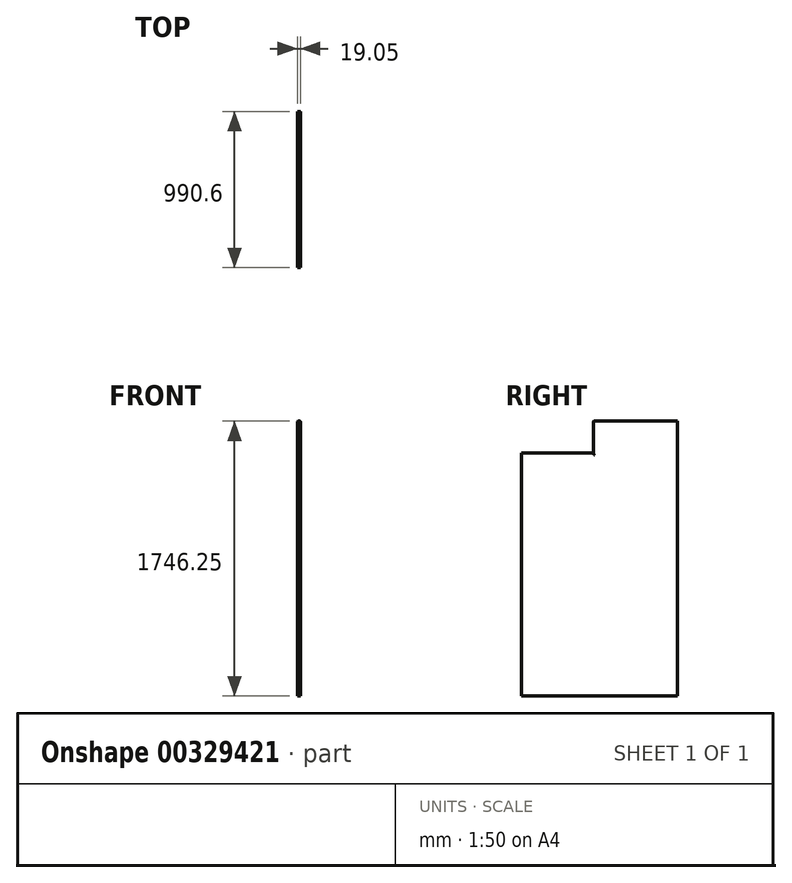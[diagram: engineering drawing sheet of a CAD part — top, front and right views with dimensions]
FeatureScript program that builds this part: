
annotation { "Feature Type Name" : "Feature", "Feature Type Description" : "" }
export const myFeature = defineFeature(function(context is Context, id is Id, definition is map)
    precondition{}
    {
        {
            var Q0;
            Q0=qCreatedBy(makeId("Right.planeOp"),FACE);
            var sketch = newSketch(context, id + "F0", { "sketchPlane" : qUnion([Q0])});
            skLineSegment(sketch, "E0.bottom", {"start": v(495.3, -771.52) * mm, "end": v(-495.3, -771.53) * mm});
            skLineSegment(sketch, "E0.top", {"start": v(-38.1, 771.53) * mm, "end": v(-495.3, 771.52) * mm});
            skLineSegment(sketch, "E0.left", {"start": v(495.3, -771.52) * mm, "end": v(495.3, 771.53) * mm});
            skLineSegment(sketch, "E0.right", {"start": v(-495.3, -771.53) * mm, "end": v(-495.3, 771.52) * mm});
            skPoint(sketch, "E0.middle", {"position": v(0, 0) * mm});
            skLineSegment(sketch, "E1", {"start": v(-495.3, 771.52) * mm, "end": v(-38.1, 771.53) * mm, "construction": true});
            skLineSegment(sketch, "E2.top", {"start": v(-38.1, 974.73) * mm, "end": v(495.3, 974.73) * mm});
            skLineSegment(sketch, "E2.left", {"start": v(-38.1, 771.52) * mm, "end": v(-38.1, 974.73) * mm});
            skLineSegment(sketch, "E2.right", {"start": v(495.3, 771.53) * mm, "end": v(495.3, 974.73) * mm});
            skSolve(sketch);
        }
        {
            var Q0;
            Q0 = qSketchRegion(id + "F0", true);
            extrude(context, id + "F1", {"entities" : qUnion([Q0]), "depth" : 19.05 * mm});
        }
        {
            var Q0;
            Q0=makeQuery(id+"F1.opExtrude","CAP_EDGE",EDGE,{"disambiguationData":[OSD([sQuery(id+"F0.wireOp",EDGE,"E0.top")])],"isStart":false});
            fillet(context, id + "F2", {"entities" : qUnion([Q0]), "radius" : 12.7 * mm, "tangentPropagation" : true, "allowEdgeOverflow" : false});
        }
        {
            var Q0;
            Q0=makeQuery(id+"F1.opExtrude","CAP_EDGE",EDGE,{"disambiguationData":[OSD([sQuery(id+"F0.wireOp",EDGE,"E2.top")])],"isStart":false});
            var Q1;
            Q1=makeQuery(id+"F1.opExtrude","CAP_EDGE",EDGE,{"disambiguationData":[OSD([sQuery(id+"F0.wireOp",EDGE,"E2.top")])],"isStart":true});
            fillet(context, id + "F3", {"entities" : qUnion([Q0, Q1]), "radius" : 6.35 * mm, "tangentPropagation" : true, "allowEdgeOverflow" : false});
        }
        {
            var Q0;
            Q0=makeQuery(id+"F1.opExtrude","CAP_EDGE",EDGE,{"disambiguationData":[OSD([sQuery(id+"F0.wireOp",EDGE,"E2.left")])],"isStart":false});
            var Q1;
            Q1=makeQuery(id+"F1.opExtrude","CAP_EDGE",EDGE,{"disambiguationData":[OSD([sQuery(id+"F0.wireOp",EDGE,"E2.left")])],"isStart":true});
            fillet(context, id + "F4", {"entities" : qUnion([Q0, Q1]), "radius" : 6.35 * mm, "tangentPropagation" : true, "allowEdgeOverflow" : false});
        }
    });
